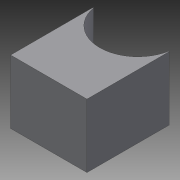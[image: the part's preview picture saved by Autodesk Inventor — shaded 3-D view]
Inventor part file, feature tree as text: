
AUTODESK INVENTOR PART (.ipt)
format: ipt  version: 2015 (Build 190159000, 159)  size: 91,136 bytes
history: native  units: mm
features: extrude x3, sketch x3, other x1, fillet x1
ambient origin geometry x8: Origin, YZ Plane, XZ Plane, XY Plane, X Axis, Y Axis, Z Axis, Center Point
bodies: Body1 (feature_tree)
feature tree (8):
  other  "ソリッド1"
  extrude  "押し出し1"  Depth=24.0mm
  extrude  "押し出し2"  Depth=53.0mm
  extrude  "押し出し3"  Depth=20.0mm TaperAngle=0.0deg
  fillet  "フィレット1"  Radius=24.0mm
  sketch  "スケッチ1"
  sketch  "スケッチ2"
  sketch  "スケッチ3"
